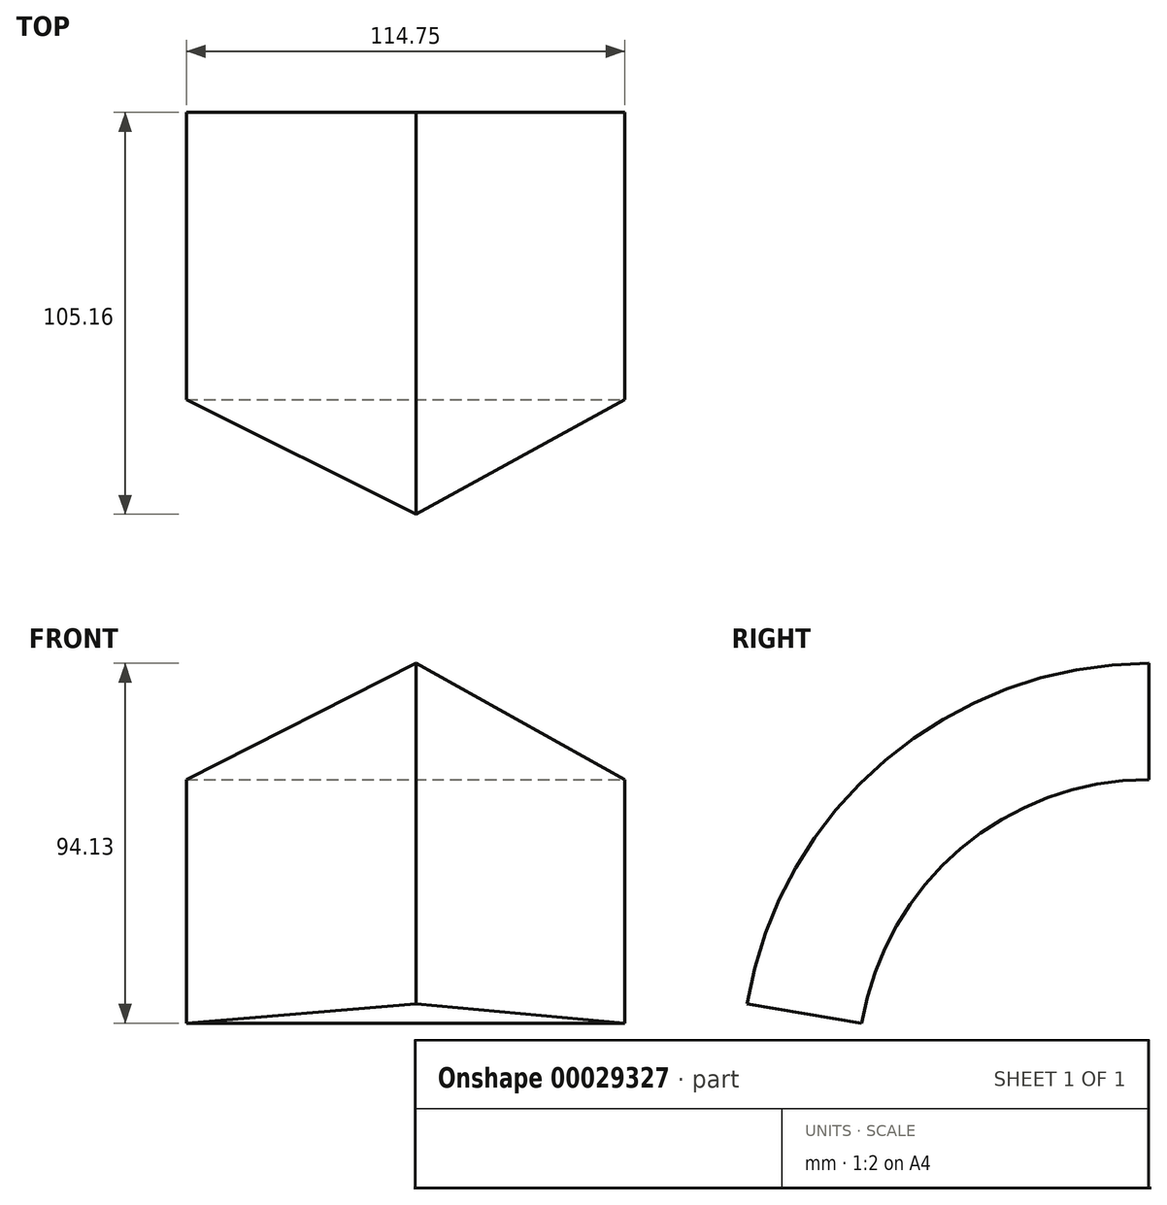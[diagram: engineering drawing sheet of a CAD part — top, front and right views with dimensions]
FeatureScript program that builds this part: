
annotation { "Feature Type Name" : "Feature", "Feature Type Description" : "" }
export const myFeature = defineFeature(function(context is Context, id is Id, definition is map)
    precondition{}
    {
        {
            var Q0;
            Q0=qCreatedBy(makeId("Front.planeOp"),FACE);
            var sketch = newSketch(context, id + "F0", { "sketchPlane" : qUnion([Q0])});
            skLineSegment(sketch, "E0", {"start": v(0, 0) * mm, "end": v(114.75, 0) * mm});
            skLineSegment(sketch, "E1", {"start": v(114.75, 0) * mm, "end": v(60.13, 30.4) * mm});
            skLineSegment(sketch, "E2", {"start": v(60.13, 30.4) * mm, "end": v(0, 0) * mm});
            skSolve(sketch);
        }
        {
            var Q0;
            Q0 = qSketchRegion(id + "F0", true);
            extrude(context, id + "F1", {"entities" : qUnion([Q0]), "depth" : 12.7 * mm});
        }
        {
            var Q0;
            Q0=makeQuery(id+"F1.opExtrude","SWEPT_FACE",FACE,{"disambiguationData":[OSD([sQuery(id+"F0.wireOp",EDGE,"E0")])]});
            var sketch = newSketch(context, id + "F2", { "sketchPlane" : qUnion([Q0])});
            skLineSegment(sketch, "E3", {"start": v(57.38, 0) * mm, "end": v(57.38, 12.7) * mm});
            skSolve(sketch);
        }
        {
            var Q0;
            Q0 = qSketchRegion(id + "F2", true);
            var Q1;
            {var subQ2=sQuery(id+"F2.wireOp",EDGE,"E3");Q1=makeQuery(id+"F2.imprint","IMPRINT",FACE,{"disambiguationData":[TD([[makeQuery(id+"F2.imprint","IMPRINT",EDGE,{"derivedFrom":subQ2}),-1.0]])]});}
            extrude(context, id + "F3", {"entities" : qUnion([Q0, Q1]), "operationType" : NewBodyOperationType.ADD, "depth" : 76.2 * mm});
        }
        {
            var Q0;
            Q0=makeQuery(id+"F3.opExtrude","SWEPT_FACE",FACE,{"disambiguationData":[OSD([sQuery(id+"F2.wireOp",EDGE,"E3")])]});
            var sketch = newSketch(context, id + "F4", { "sketchPlane" : qUnion([Q0])});
            skArc(sketch, "E4", {"start": v(87.87, -63.73) * mm, "mid": v(61.98, -18.08) * mm, "end": v(12.7, 0) * mm});
            skArc(sketch, "E5", {"start": v(12.7, 0) * mm, "mid": v(-36.58, -134.32) * mm, "end": v(87.87, -63.73) * mm});
            skSolve(sketch);
        }
        {
            var Q0;
            Q0=makeQuery(id+"F3.opExtrude","CAP_FACE",FACE,{"disambiguationData":[OSD([sQuery(id+"F0.wireOp",EDGE,"E0"),sQuery(id+"F0.wireOp",EDGE,"E1"),sQuery(id+"F2.wireOp",EDGE,"E3")])],"isStart":false});
            extrude(context, id + "F5", {"entities" : qUnion([Q0]), "operationType" : NewBodyOperationType.REMOVE, "oppositeDirection" : true, "depth" : 76.2 * mm});
        }
        {
            var Q0;
            {var subQ0=sQuery(id+"F0.wireOp",EDGE,"E0");var subQ1=sQuery(id+"F0.wireOp",EDGE,"E1");var subQ2=makeQuery(id+"F1.opExtrude","CAP_EDGE",EDGE,{"disambiguationData":[OSD([subQ0])],"isStart":false});Q0=makeQuery(id+"F3.boolean.opBoolean","MERGE",FACE,{"derivedFrom":[makeQuery(id+"F1.opExtrude","CAP_FACE",FACE,{"disambiguationData":[OSD([subQ0,subQ1,sQuery(id+"F0.wireOp",EDGE,"E2")])],"isStart":false}),makeQuery(id+"F3.opExtrude","SWEPT_FACE",FACE,{"disambiguationData":[OSD([subQ0]),TDD([makeQuery(id+"F2.imprint","IMPRINT",EDGE,{"disambiguationData":[TD([[makeQuery(id+"F2.imprint","INTERSECT",VERTEX,{"derivedFrom":[subQ2,sQuery(id+"F2.wireOp",EDGE,"E3")]}),-1.0]])],"derivedFrom":subQ2})])]})]});}
            var Q1;
            Q1=sQuery(id+"F4.wireOp",EDGE,"E4");
            sweep(context, id + "F6", {"operationType" : NewBodyOperationType.ADD, "profiles" : qUnion([Q0]), "path" : qUnion([Q1])});
        }
        {
            var Q0;
            {var subQ0=sQuery(id+"F0.wireOp",EDGE,"E0");var subQ1=sQuery(id+"F0.wireOp",EDGE,"E1");var subQ2=makeQuery(id+"F1.opExtrude","CAP_EDGE",EDGE,{"disambiguationData":[OSD([subQ0])],"isStart":true});Q0=makeQuery(id+"F3.boolean.opBoolean","MERGE",FACE,{"derivedFrom":[makeQuery(id+"F1.opExtrude","CAP_FACE",FACE,{"disambiguationData":[OSD([subQ0,subQ1,sQuery(id+"F0.wireOp",EDGE,"E2")])],"isStart":true}),makeQuery(id+"F3.opExtrude","SWEPT_FACE",FACE,{"disambiguationData":[OSD([subQ0]),TDD([makeQuery(id+"F2.imprint","IMPRINT",EDGE,{"disambiguationData":[TD([[makeQuery(id+"F2.imprint","INTERSECT",VERTEX,{"derivedFrom":[subQ2,sQuery(id+"F2.wireOp",EDGE,"E3")]}),-1.0]])],"derivedFrom":subQ2})])]})]});}
            extrude(context, id + "F7", {"entities" : qUnion([Q0]), "operationType" : NewBodyOperationType.REMOVE, "oppositeDirection" : true, "depth" : 12.7 * mm});
        }
    });
